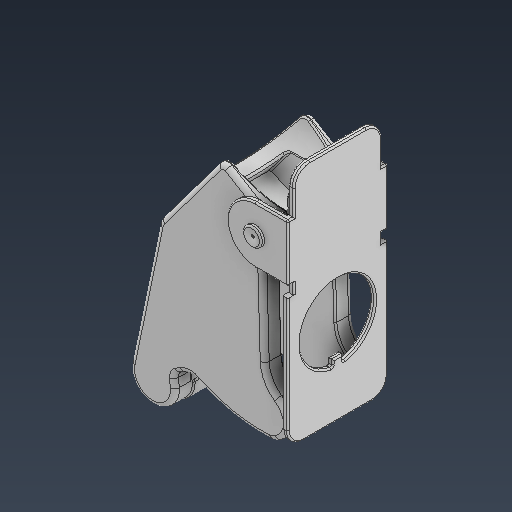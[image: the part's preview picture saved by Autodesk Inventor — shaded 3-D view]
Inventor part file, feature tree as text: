
AUTODESK INVENTOR PART (.ipt)
format: ipt  version: 2025.3 (Build 293356000, 356)  size: 946,688 bytes
history: native  units: in
note: dims shown in document units (in); Inventor stores cm internally (conversion verified against a paired STEP export)
features: fillet x3, other x3
ambient origin geometry x8: Origin, YZ Plane, XZ Plane, XY Plane, X Axis, Y Axis, Z Axis, Center Point
bodies: Solid1 (feature_tree), Solid2 (feature_tree), Solid3 (feature_tree), Solid4 (feature_tree), Solid5 (feature_tree), Solid6 (feature_tree)
feature tree (6):
  fillet  "Fillet7"  [1 undecoded]
  fillet  "Fillet8"  [1 undecoded]
  other  "Body-Move_Copy3"
  other  "Body-Move_Copy6"
  other  "Cut-Extrude6"
  fillet  "Fillet19"  [1 undecoded]
note: 3 required parameter values undecoded (feature->parameter linkage not recoverable at this tier; creation-order binding heuristic only, values carry confidence <= 0.55)
